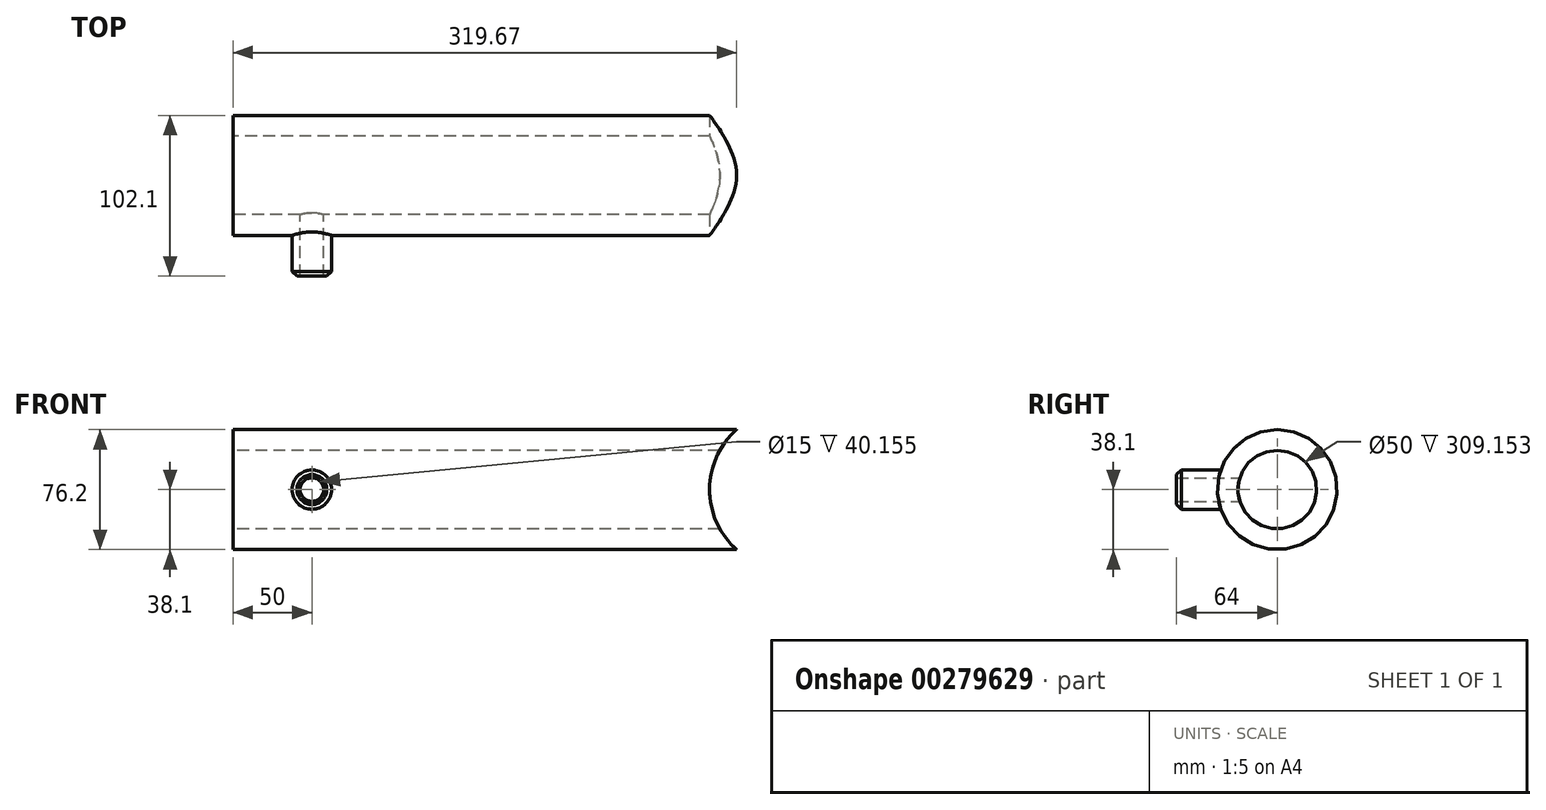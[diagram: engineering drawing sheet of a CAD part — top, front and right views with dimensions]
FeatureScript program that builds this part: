
annotation { "Feature Type Name" : "Feature", "Feature Type Description" : "" }
export const myFeature = defineFeature(function(context is Context, id is Id, definition is map)
    precondition{}
    {
        {
            var Q0;
            Q0=qCreatedBy(makeId("Front.planeOp"),FACE);
            var sketch = newSketch(context, id + "F0", { "sketchPlane" : qUnion([Q0])});
            skCircle(sketch, "E0", {"center": v(0, 0) * mm, "radius": 7.5 * mm});
            skCircle(sketch, "E1", {"center": v(0, 0) * mm, "radius": 12.5 * mm});
            skSolve(sketch);
        }
        {
            var Q0;
            Q0 = qSketchRegion(id + "F0", true);
            extrude(context, id + "F1", {"entities" : qUnion([Q0]), "depth" : 64 * mm});
        }
        {
            var Q0;
            Q0=qCreatedBy(makeId("Right.planeOp"),FACE);
            var sketch = newSketch(context, id + "F2", { "sketchPlane" : qUnion([Q0])});
            skCircle(sketch, "E2", {"center": v(0, 0) * mm, "radius": 38.1 * mm});
            skCircle(sketch, "E3", {"center": v(0, 0) * mm, "radius": 25 * mm});
            skSolve(sketch);
        }
        {
            var Q0;
            Q0 = qSketchRegion(id + "F2", true);
            extrude(context, id + "F3", {"entities" : qUnion([Q0]), "operationType" : NewBodyOperationType.ADD, "depth" : 100 * mm});
        }
        {
            var Q0;
            Q0 = qSketchRegion(id + "F2", true);
            extrude(context, id + "F4", {"entities" : qUnion([Q0]), "operationType" : NewBodyOperationType.ADD, "oppositeDirection" : true, "depth" : 50 * mm});
        }
        {
            var Q0;
            Q0=makeQuery(id+"F1.opExtrude","CAP_EDGE",EDGE,{"disambiguationData":[OSD([sQuery(id+"F0.wireOp",EDGE,"E1")])],"isStart":false});
            chamfer(context, id + "F5", {"entities" : qUnion([Q0]), "width" : 3 * mm, "tangentPropagation" : true});
        }
        {
            var Q0;
            Q0=makeQuery(id+"F4.opExtrude","CAP_FACE",FACE,{"disambiguationData":[OSD([sQuery(id+"F2.wireOp",EDGE,"E2"),sQuery(id+"F2.wireOp",EDGE,"E3")])],"isStart":false});
            var sketch = newSketch(context, id + "F6", { "sketchPlane" : qUnion([Q0])});
            skCircle(sketch, "E4", {"center": v(0, 0) * mm, "radius": 25 * mm});
            skSolve(sketch);
        }
        {
            var Q0;
            Q0 = qSketchRegion(id + "F6", true);
            extrude(context, id + "F7", {"entities" : qUnion([Q0]), "operationType" : NewBodyOperationType.REMOVE, "oppositeDirection" : true, "depth" : 200 * mm});
        }
        {
            var Q0;
            Q0=makeQuery(id+"F1.opExtrude","CAP_FACE",FACE,{"disambiguationData":[OSD([sQuery(id+"F0.wireOp",EDGE,"E0"),sQuery(id+"F0.wireOp",EDGE,"E1")])],"isStart":false});
            var sketch = newSketch(context, id + "F8", { "sketchPlane" : qUnion([Q0])});
            skCircle(sketch, "E5", {"center": v(0, 0) * mm, "radius": 7.5 * mm});
            skSolve(sketch);
        }
        {
            var Q0;
            Q0 = qSketchRegion(id + "F8", true);
            extrude(context, id + "F9", {"entities" : qUnion([Q0]), "operationType" : NewBodyOperationType.REMOVE, "oppositeDirection" : true, "depth" : 50 * mm});
        }
        {
            var Q0;
            Q0=makeQuery(id+"F3.opExtrude","CAP_FACE",FACE,{"disambiguationData":[OSD([sQuery(id+"F2.wireOp",EDGE,"E2"),sQuery(id+"F2.wireOp",EDGE,"E3")])],"isStart":false});
            extrude(context, id + "F10", {"entities" : qUnion([Q0]), "operationType" : NewBodyOperationType.ADD, "depth" : 100 * mm});
        }
        {
            var Q0;
            Q0=makeQuery(id+"F1.opExtrude","CAP_FACE",FACE,{"disambiguationData":[OSD([sQuery(id+"F0.wireOp",EDGE,"E0"),sQuery(id+"F0.wireOp",EDGE,"E1")])],"isStart":false});
            var sketch = newSketch(context, id + "F11", { "sketchPlane" : qUnion([Q0])});
            skCircle(sketch, "E6", {"center": v(0, 0) * mm, "radius": 7.5 * mm});
            skSolve(sketch);
        }
        {
            var Q0;
            Q0 = qSketchRegion(id + "F11", true);
            extrude(context, id + "F12", {"entities" : qUnion([Q0]), "operationType" : NewBodyOperationType.REMOVE, "oppositeDirection" : true, "depth" : 50 * mm});
        }
        {
            var Q0;
            Q0=makeQuery(id+"F10.opExtrude","CAP_FACE",FACE,{"disambiguationData":[OSD([sQuery(id+"F2.wireOp",EDGE,"E2"),sQuery(id+"F2.wireOp",EDGE,"E3")])],"isStart":false});
            extrude(context, id + "F13", {"entities" : qUnion([Q0]), "operationType" : NewBodyOperationType.ADD, "depth" : 75 * mm});
        }
        {
            var Q0;
            Q0=qCreatedBy(makeId("Top.planeOp"),FACE);
            var sketch = newSketch(context, id + "F14", { "sketchPlane" : qUnion([Q0])});
            skLineSegment(sketch, "E7", {"start": v(303.7, 52.96) * mm, "end": v(303.7, -52.1) * mm, "construction": true});
            skLineSegment(sketch, "E8", {"start": v(252.61, 51.93) * mm, "end": v(252.61, -50.66) * mm});
            skLineSegment(sketch, "E9", {"start": v(252.61, -50.66) * mm, "end": v(303.7, -52.1) * mm});
            skLineSegment(sketch, "E10", {"start": v(252.61, 51.93) * mm, "end": v(303.7, 52.96) * mm});
            skLineSegment(sketch, "E11", {"start": v(280.14, -51.43) * mm, "end": v(280.14, 52.96) * mm});
            skSolve(sketch);
        }
        {
            var Q0;
            {var subQ0=sQuery(id+"F14.wireOp",EDGE,"E8");Q0=makeQuery(id+"F14.imprint","IMPRINT",FACE,{"disambiguationData":[TD([[makeQuery(id+"F14.imprint","IMPRINT",EDGE,{"derivedFrom":subQ0}),1.0]])]});}
            var Q1;
            Q1=sQuery(id+"F14.wireOp",EDGE,"E7");
            revolve(context, id + "F15", {"operationType" : NewBodyOperationType.REMOVE, "entities" : qUnion([Q0]), "axis" : qUnion([Q1]), "revolveType" : RevolveType.FULL, "oppositeDirection" : true});
        }
    });
